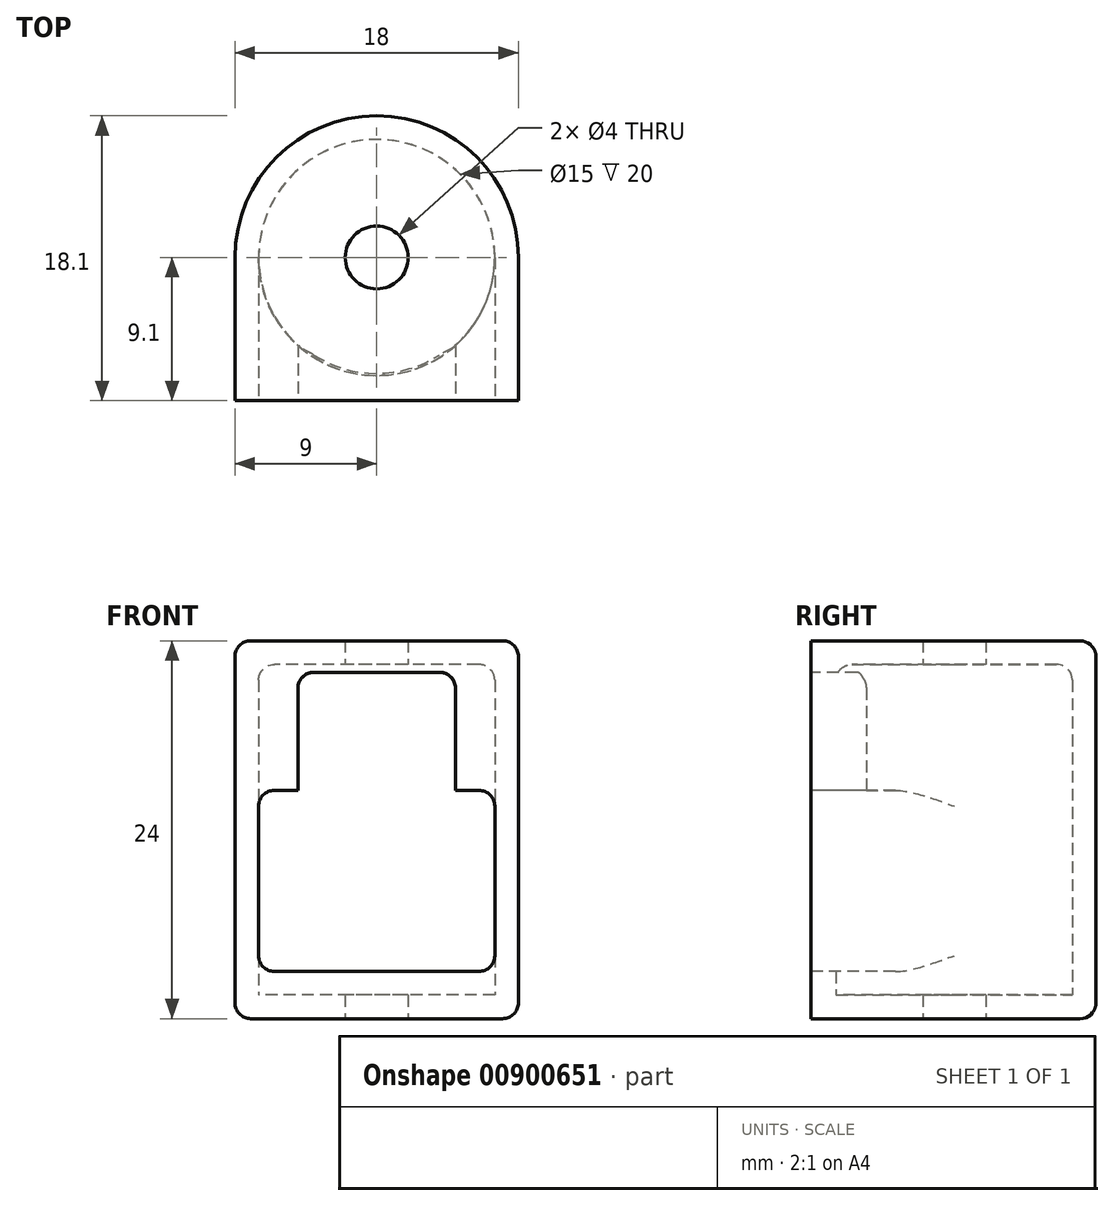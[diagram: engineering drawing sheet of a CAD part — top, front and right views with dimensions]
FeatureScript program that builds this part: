
annotation { "Feature Type Name" : "Feature", "Feature Type Description" : "" }
export const myFeature = defineFeature(function(context is Context, id is Id, definition is map)
    precondition{}
    {
        {
            var Q0;
            Q0=qCreatedBy(makeId("Top.planeOp"),FACE);
            var sketch = newSketch(context, id + "F0", { "sketchPlane" : qUnion([Q0])});
            skCircle(sketch, "E0", {"center": v(0, 0) * mm, "radius": 7.5 * mm});
            skCircle(sketch, "E1", {"center": v(0, 0) * mm, "radius": 9 * mm});
            skPoint(sketch, "E2", {"position": v(7.5, 0) * mm});
            skLineSegment(sketch, "E3", {"start": v(0, -9) * mm, "end": v(0, -9.1) * mm});
            skCircle(sketch, "E4", {"center": v(0, 0) * mm, "radius": 2 * mm});
            skSolve(sketch);
        }
        {
            var Q0;
            Q0=qCreatedBy(makeId("Front.planeOp"),FACE);
            var Q1;
            Q1=sQuery(id+"F0.wireOp",VERTEX,"E3.end");
            cPlane(context, id + "F1", {"entities" : qUnion([Q0, Q1]), "cplaneType" : CPlaneType.PLANE_POINT, "offset" : 25 * mm, "width" : 150 * mm, "height" : 150 * mm});
        }
        {
            var Q0;
            Q0=qCreatedBy(id+"F1.planeOp",FACE);
            var sketch = newSketch(context, id + "F2", { "sketchPlane" : qUnion([Q0])});
            skLineSegment(sketch, "E5.bottom", {"start": v(-9, 12) * mm, "end": v(9, 12) * mm});
            skLineSegment(sketch, "E5.top", {"start": v(-9, -12) * mm, "end": v(9, -12) * mm});
            skLineSegment(sketch, "E5.left", {"start": v(-9, 12) * mm, "end": v(-9, -12) * mm});
            skLineSegment(sketch, "E5.right", {"start": v(9, 12) * mm, "end": v(9, -12) * mm});
            skLineSegment(sketch, "E6.bottom", {"start": v(7.5, -10.5) * mm, "end": v(-7.5, -10.5) * mm});
            skLineSegment(sketch, "E6.top", {"start": v(7.5, 10.5) * mm, "end": v(-7.5, 10.5) * mm});
            skLineSegment(sketch, "E6.left", {"start": v(7.5, -10.5) * mm, "end": v(7.5, 10.5) * mm});
            skLineSegment(sketch, "E6.right", {"start": v(-7.5, -10.5) * mm, "end": v(-7.5, 10.5) * mm});
            skLineSegment(sketch, "E7.bottom", {"start": v(-7.5, 2.5) * mm, "end": v(7.5, 2.5) * mm});
            skLineSegment(sketch, "E8", {"start": v(-5, 10) * mm, "end": v(-5, 2.5) * mm});
            skLineSegment(sketch, "E9", {"start": v(5, 10) * mm, "end": v(5, 2.5) * mm});
            skLineSegment(sketch, "E10", {"start": v(0, 10.5) * mm, "end": v(0, 2.5) * mm, "construction": true});
            skLineSegment(sketch, "E11", {"start": v(-5, 10) * mm, "end": v(5, 10) * mm});
            skLineSegment(sketch, "E12", {"start": v(-5, 10) * mm, "end": v(-5, 10.5) * mm});
            skLineSegment(sketch, "E13", {"start": v(5, 10) * mm, "end": v(5, 10.5) * mm});
            skLineSegment(sketch, "E14", {"start": v(-7.5, -9) * mm, "end": v(7.5, -9) * mm});
            skSolve(sketch);
        }
        {
            var Q0;
            Q0=makeQuery(id+"F0.imprint","IMPRINT",FACE,{"disambiguationData":[TD([[makeQuery(id+"F0.imprint","IMPRINT",EDGE,{"derivedFrom":sQuery(id+"F0.wireOp",EDGE,"E0")}),1.0]])]});
            var Q1;
            Q1=makeQuery(id+"F0.imprint","IMPRINT",FACE,{"disambiguationData":[TD([[makeQuery(id+"F0.imprint","IMPRINT",EDGE,{"derivedFrom":sQuery(id+"F0.wireOp",EDGE,"E0")}),-1.0]])]});
            var Q2;
            Q2=sQuery(id+"F2.wireOp",VERTEX,"E5.bottom.end");
            var Q3;
            Q3=sQuery(id+"F2.wireOp",VERTEX,"E5.top.end");
            extrude(context, id + "F3", {"entities" : qUnion([Q0, Q1]), "endBound" : BoundingType.UP_TO_VERTEX, "depth" : 24 * mm, "endBoundEntityVertex" : qUnion([Q2]), "offsetDistance" : 25 * mm, "hasSecondDirection" : true, "secondDirectionBound" : SecondDirectionBoundingType.UP_TO_VERTEX, "secondDirectionOppositeDirection" : true, "secondDirectionDepth" : 25 * mm, "secondDirectionBoundEntityVertex" : qUnion([Q3])});
        }
        {
            var Q0;
            Q0=makeQuery(id+"F0.imprint","IMPRINT",FACE,{"disambiguationData":[TD([[makeQuery(id+"F0.imprint","IMPRINT",EDGE,{"derivedFrom":sQuery(id+"F0.wireOp",EDGE,"E0")}),1.0]])]});
            var Q1;
            Q1=sQuery(id+"F2.wireOp",VERTEX,"E6.top.start");
            var Q2;
            Q2=sQuery(id+"F2.wireOp",VERTEX,"E6.bottom.start");
            extrude(context, id + "F4", {"entities" : qUnion([Q0]), "operationType" : NewBodyOperationType.REMOVE, "endBound" : BoundingType.UP_TO_VERTEX, "depth" : 21 * mm, "endBoundEntityVertex" : qUnion([Q1]), "offsetDistance" : 25 * mm, "hasSecondDirection" : true, "secondDirectionBound" : SecondDirectionBoundingType.UP_TO_VERTEX, "secondDirectionOppositeDirection" : true, "secondDirectionDepth" : 25 * mm, "secondDirectionBoundEntityVertex" : qUnion([Q2])});
        }
        {
            var Q0;
            Q0=makeQuery(id+"F4.boolean.opBoolean","COPY",EDGE,{"derivedFrom":makeQuery(id+"F4.opExtrude","CAP_EDGE",EDGE,{"disambiguationData":[OSD([sQuery(id+"F0.wireOp",EDGE,"E0")])],"isStart":false})});
            fillet(context, id + "F5", {"entities" : qUnion([Q0]), "radius" : 1 * mm, "tangentPropagation" : true, "allowEdgeOverflow" : false});
        }
        {
            var Q0;
            {var subQ0=sQuery(id+"F2.wireOp",EDGE,"E8");Q0=makeQuery(id+"F2.imprint","IMPRINT",FACE,{"disambiguationData":[TD([[makeQuery(id+"F2.imprint","IMPRINT",EDGE,{"derivedFrom":subQ0}),1.0]])]});}
            var Q1;
            {var subQ5=sQuery(id+"F2.wireOp",EDGE,"E14");Q1=makeQuery(id+"F2.imprint","IMPRINT",FACE,{"disambiguationData":[TD([[makeQuery(id+"F2.imprint","IMPRINT",EDGE,{"derivedFrom":subQ5}),1.0]])]});}
            var Q2;
            Q2=sQuery(id+"F0.wireOp",VERTEX,"E0.center");
            extrude(context, id + "F6", {"entities" : qUnion([Q0, Q1]), "operationType" : NewBodyOperationType.REMOVE, "endBound" : BoundingType.UP_TO_VERTEX, "oppositeDirection" : true, "depth" : 25 * mm, "endBoundEntityVertex" : qUnion([Q2]), "offsetDistance" : 25 * mm});
        }
        {
            var Q0;
            Q0=makeQuery(id+"F2.imprint","IMPRINT",FACE,{"disambiguationData":[TD([[makeQuery(id+"F2.imprint","IMPRINT",EDGE,{"derivedFrom":sQuery(id+"F2.wireOp",EDGE,"E5.bottom")}),-1.0]])]});
            var Q1;
            {var subQ0=sQuery(id+"F2.wireOp",EDGE,"E8");Q1=makeQuery(id+"F2.imprint","IMPRINT",FACE,{"disambiguationData":[TD([[makeQuery(id+"F2.imprint","IMPRINT",EDGE,{"derivedFrom":subQ0}),-1.0]])]});}
            var Q2;
            Q2=makeQuery(id+"F2.imprint","IMPRINT",FACE,{"disambiguationData":[TD([[makeQuery(id+"F2.imprint","IMPRINT",EDGE,{"derivedFrom":sQuery(id+"F2.wireOp",EDGE,"E11")}),1.0]])]});
            var Q3;
            {var subQ0=sQuery(id+"F2.wireOp",EDGE,"E6.bottom");Q3=makeQuery(id+"F2.imprint","IMPRINT",FACE,{"disambiguationData":[TD([[makeQuery(id+"F2.imprint","IMPRINT",EDGE,{"derivedFrom":subQ0}),-1.0]])]});}
            var Q4;
            {var subQ0=sQuery(id+"F2.wireOp",EDGE,"E9");Q4=makeQuery(id+"F2.imprint","IMPRINT",FACE,{"disambiguationData":[TD([[makeQuery(id+"F2.imprint","IMPRINT",EDGE,{"derivedFrom":subQ0}),1.0]])]});}
            var Q5;
            Q5=makeQuery(id+"F3.opExtrude","SWEPT_FACE",FACE,{"disambiguationData":[OSD([sQuery(id+"F0.wireOp",EDGE,"E1")])]});
            extrude(context, id + "F7", {"entities" : qUnion([Q0, Q1, Q2, Q3, Q4]), "operationType" : NewBodyOperationType.ADD, "endBound" : BoundingType.UP_TO_SURFACE, "oppositeDirection" : true, "depth" : 9 * mm, "endBoundEntityFace" : qUnion([Q5]), "offsetDistance" : 25 * mm});
        }
        {
            var Q0;
            {var subQ0=sQuery(id+"F2.wireOp",EDGE,"E12");var subQ1=sQuery(id+"F2.wireOp",EDGE,"E11");var subQ2=sQuery(id+"F2.wireOp",EDGE,"E8");Q0=makeQuery(id+"F7.boolean.opBoolean","MERGE",EDGE,{"derivedFrom":[makeQuery(id+"F6.boolean.opBoolean","COPY",EDGE,{"derivedFrom":makeQuery(id+"F6.opExtrude","SWEPT_EDGE",EDGE,{"disambiguationData":[OSD([subQ2,subQ1,subQ0])]})}),makeQuery(id+"F7.opExtrude","SWEPT_EDGE",EDGE,{"disambiguationData":[OSD([subQ2,subQ1,subQ0])]})]});}
            var Q1;
            {var subQ0=sQuery(id+"F2.wireOp",EDGE,"E13");var subQ1=sQuery(id+"F2.wireOp",EDGE,"E11");var subQ2=sQuery(id+"F2.wireOp",EDGE,"E9");Q1=makeQuery(id+"F7.boolean.opBoolean","MERGE",EDGE,{"derivedFrom":[makeQuery(id+"F6.boolean.opBoolean","COPY",EDGE,{"derivedFrom":makeQuery(id+"F6.opExtrude","SWEPT_EDGE",EDGE,{"disambiguationData":[OSD([subQ2,subQ1,subQ0])]})}),makeQuery(id+"F7.opExtrude","SWEPT_EDGE",EDGE,{"disambiguationData":[OSD([subQ2,subQ1,subQ0])]})]});}
            var Q2;
            {var subQ0=sQuery(id+"F2.wireOp",EDGE,"E7.bottom");var subQ1=sQuery(id+"F2.wireOp",EDGE,"E6.left");Q2=makeQuery(id+"F7.boolean.opBoolean","MERGE",EDGE,{"derivedFrom":[makeQuery(id+"F6.boolean.opBoolean","COPY",EDGE,{"derivedFrom":makeQuery(id+"F6.opExtrude","SWEPT_EDGE",EDGE,{"disambiguationData":[OSD([subQ1,subQ0])]})}),makeQuery(id+"F7.opExtrude","SWEPT_EDGE",EDGE,{"disambiguationData":[OSD([subQ1,subQ0])]})]});}
            var Q3;
            {var subQ0=sQuery(id+"F2.wireOp",EDGE,"E7.bottom");var subQ1=sQuery(id+"F2.wireOp",EDGE,"E6.right");Q3=makeQuery(id+"F7.boolean.opBoolean","MERGE",EDGE,{"derivedFrom":[makeQuery(id+"F6.boolean.opBoolean","COPY",EDGE,{"derivedFrom":makeQuery(id+"F6.opExtrude","SWEPT_EDGE",EDGE,{"disambiguationData":[OSD([subQ1,subQ0])]})}),makeQuery(id+"F7.opExtrude","SWEPT_EDGE",EDGE,{"disambiguationData":[OSD([subQ1,subQ0])]})]});}
            var Q4;
            {var subQ0=sQuery(id+"F2.wireOp",EDGE,"E14");var subQ1=sQuery(id+"F2.wireOp",EDGE,"E6.left");Q4=makeQuery(id+"F7.boolean.opBoolean","MERGE",EDGE,{"derivedFrom":[makeQuery(id+"F6.boolean.opBoolean","COPY",EDGE,{"derivedFrom":makeQuery(id+"F6.opExtrude","SWEPT_EDGE",EDGE,{"disambiguationData":[OSD([subQ1,subQ0])]})}),makeQuery(id+"F7.opExtrude","SWEPT_EDGE",EDGE,{"disambiguationData":[OSD([subQ1,subQ0])]})]});}
            var Q5;
            {var subQ0=sQuery(id+"F2.wireOp",EDGE,"E14");var subQ1=sQuery(id+"F2.wireOp",EDGE,"E6.right");Q5=makeQuery(id+"F7.boolean.opBoolean","MERGE",EDGE,{"derivedFrom":[makeQuery(id+"F6.boolean.opBoolean","COPY",EDGE,{"derivedFrom":makeQuery(id+"F6.opExtrude","SWEPT_EDGE",EDGE,{"disambiguationData":[OSD([subQ1,subQ0])]})}),makeQuery(id+"F7.opExtrude","SWEPT_EDGE",EDGE,{"disambiguationData":[OSD([subQ1,subQ0])]})]});}
            var Q6;
            Q6=makeQuery(id+"F7.opExtrude","SWEPT_EDGE",EDGE,{"disambiguationData":[OSD([sQuery(id+"F2.wireOp",EDGE,"E5.top"),sQuery(id+"F2.wireOp",EDGE,"E5.right")])]});
            var Q7;
            Q7=makeQuery(id+"F7.opExtrude","SWEPT_EDGE",EDGE,{"disambiguationData":[OSD([sQuery(id+"F2.wireOp",EDGE,"E5.bottom"),sQuery(id+"F2.wireOp",EDGE,"E5.right")])]});
            fillet(context, id + "F8", {"entities" : qUnion([Q0, Q1, Q2, Q3, Q4, Q5, Q6, Q7]), "radius" : 1 * mm, "tangentPropagation" : true, "allowEdgeOverflow" : false});
        }
    });
